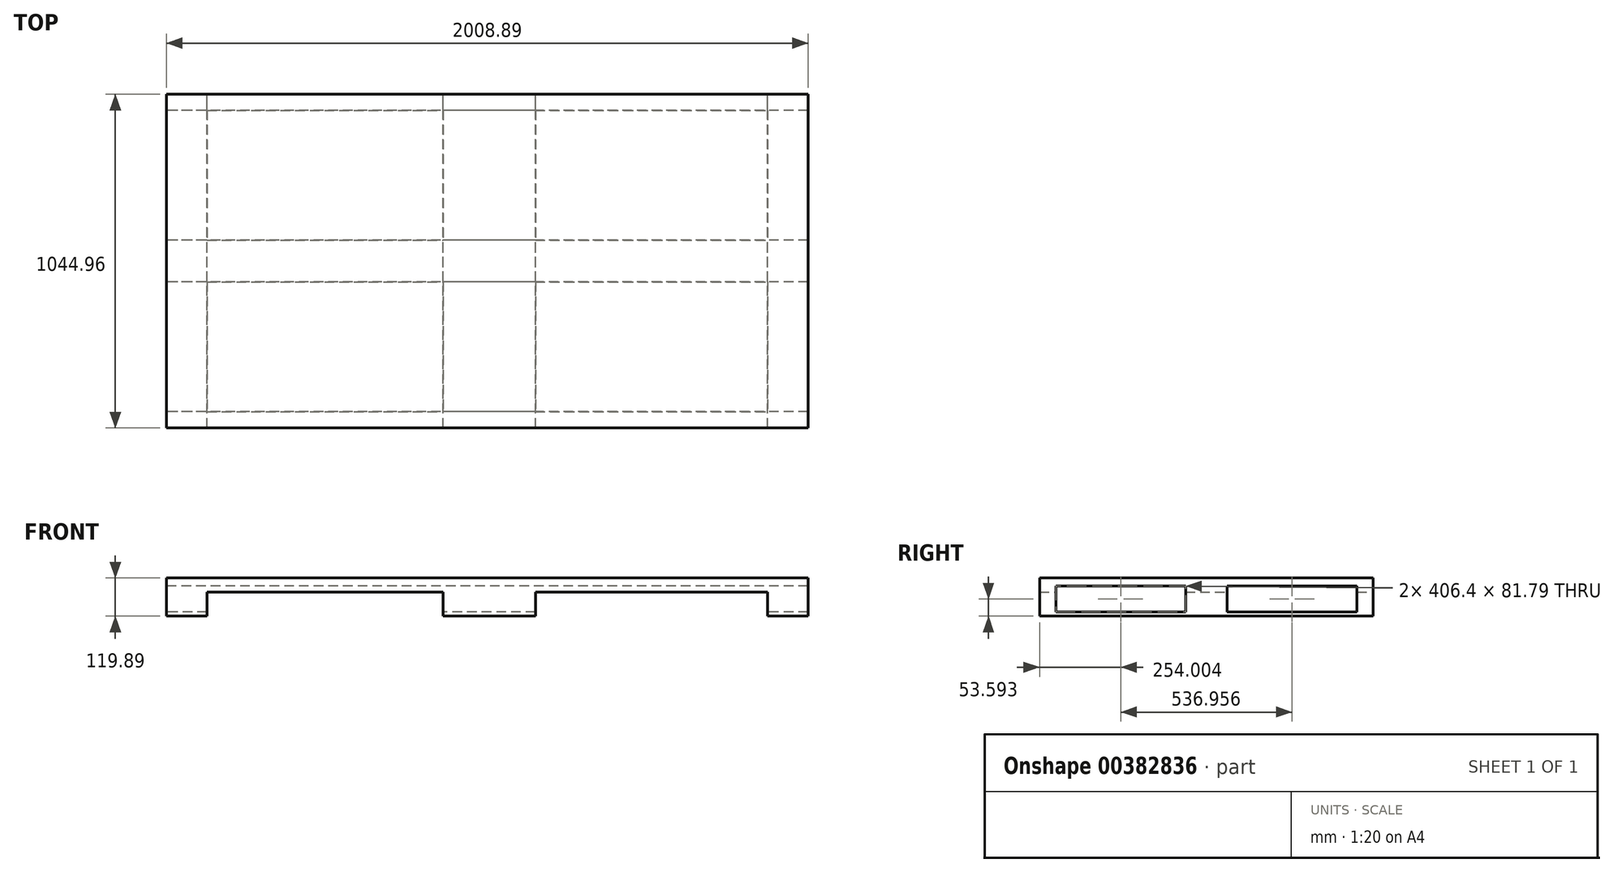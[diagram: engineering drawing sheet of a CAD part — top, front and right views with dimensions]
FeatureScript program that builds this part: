
annotation { "Feature Type Name" : "Feature", "Feature Type Description" : "" }
export const myFeature = defineFeature(function(context is Context, id is Id, definition is map)
    precondition{}
    {
        {
            var Q0;
            Q0=qCreatedBy(makeId("Front.planeOp"),FACE);
            var sketch = newSketch(context, id + "F0", { "sketchPlane" : qUnion([Q0])});
            skLineSegment(sketch, "E0.bottom", {"start": v(-571.4, -7.16) * mm, "end": v(1437.48, -7.16) * mm});
            skLineSegment(sketch, "E0.top", {"start": v(-571.4, -127.05) * mm, "end": v(1437.48, -127.05) * mm});
            skLineSegment(sketch, "E0.left", {"start": v(-571.4, -7.16) * mm, "end": v(-571.4, -127.05) * mm});
            skLineSegment(sketch, "E0.right", {"start": v(1437.48, -7.16) * mm, "end": v(1437.48, -127.05) * mm});
            skSolve(sketch);
        }
        {
            var Q0;
            Q0 = qSketchRegion(id + "F0", true);
            extrude(context, id + "F1", {"entities" : qUnion([Q0]), "depth" : 1044.96 * mm});
        }
        {
            var Q0;
            Q0=makeQuery(id+"F1.opExtrude","CAP_FACE",FACE,{"disambiguationData":[OSD([sQuery(id+"F0.wireOp",EDGE,"E0.bottom"),sQuery(id+"F0.wireOp",EDGE,"E0.top"),sQuery(id+"F0.wireOp",EDGE,"E0.left"),sQuery(id+"F0.wireOp",EDGE,"E0.right")])],"isStart":true});
            var sketch = newSketch(context, id + "F2", { "sketchPlane" : qUnion([Q0])});
            skLineSegment(sketch, "E1.bottom", {"start": v(-1310.48, -127.05) * mm, "end": v(-583.7, -127.05) * mm});
            skLineSegment(sketch, "E1.top", {"start": v(-1310.48, -51.8) * mm, "end": v(-583.7, -51.8) * mm});
            skLineSegment(sketch, "E1.left", {"start": v(-1310.48, -127.05) * mm, "end": v(-1310.48, -51.8) * mm});
            skLineSegment(sketch, "E1.right", {"start": v(-583.7, -127.05) * mm, "end": v(-583.7, -51.8) * mm});
            skLineSegment(sketch, "E2.bottom", {"start": v(-294.42, -127.05) * mm, "end": v(444.4, -127.05) * mm});
            skLineSegment(sketch, "E2.top", {"start": v(-294.42, -51.8) * mm, "end": v(444.4, -51.8) * mm});
            skLineSegment(sketch, "E2.left", {"start": v(-294.42, -127.05) * mm, "end": v(-294.42, -51.8) * mm});
            skLineSegment(sketch, "E2.right", {"start": v(444.4, -127.05) * mm, "end": v(444.4, -51.8) * mm});
            skSolve(sketch);
        }
        {
            var Q0;
            Q0=makeQuery(id+"F2.imprint","IMPRINT",FACE,{"disambiguationData":[TD([[makeQuery(id+"F2.imprint","IMPRINT",EDGE,{"derivedFrom":sQuery(id+"F2.wireOp",EDGE,"E2.bottom")}),-1.0]])]});
            var Q1;
            Q1=makeQuery(id+"F2.imprint","IMPRINT",FACE,{"disambiguationData":[TD([[makeQuery(id+"F2.imprint","IMPRINT",EDGE,{"derivedFrom":sQuery(id+"F2.wireOp",EDGE,"E1.bottom")}),-1.0]])]});
            extrude(context, id + "F3", {"entities" : qUnion([Q0, Q1]), "operationType" : NewBodyOperationType.REMOVE, "oppositeDirection" : true, "depth" : 1044.96 * mm});
        }
        {
            var Q0;
            Q0=makeQuery(id+"F1.opExtrude","SWEPT_FACE",FACE,{"disambiguationData":[OSD([sQuery(id+"F0.wireOp",EDGE,"E0.left")])]});
            var sketch = newSketch(context, id + "F4", { "sketchPlane" : qUnion([Q0])});
            skLineSegment(sketch, "E3.bottom", {"start": v(50.8, -32.56) * mm, "end": v(457.2, -32.56) * mm});
            skLineSegment(sketch, "E3.top", {"start": v(50.8, -114.35) * mm, "end": v(457.2, -114.35) * mm});
            skLineSegment(sketch, "E3.left", {"start": v(50.8, -32.56) * mm, "end": v(50.8, -114.35) * mm});
            skLineSegment(sketch, "E3.right", {"start": v(457.2, -32.56) * mm, "end": v(457.2, -114.35) * mm});
            skLineSegment(sketch, "E4.bottom", {"start": v(587.76, -32.56) * mm, "end": v(994.16, -32.56) * mm});
            skLineSegment(sketch, "E4.top", {"start": v(587.76, -114.35) * mm, "end": v(994.16, -114.35) * mm});
            skLineSegment(sketch, "E4.left", {"start": v(587.76, -32.56) * mm, "end": v(587.76, -114.35) * mm});
            skLineSegment(sketch, "E4.right", {"start": v(994.16, -32.56) * mm, "end": v(994.16, -114.35) * mm});
            skSolve(sketch);
        }
        {
            var Q0;
            Q0 = qSketchRegion(id + "F4", true);
            extrude(context, id + "F5", {"entities" : qUnion([Q0]), "operationType" : NewBodyOperationType.REMOVE, "oppositeDirection" : true, "depth" : 2008.9 * mm});
        }
    });
